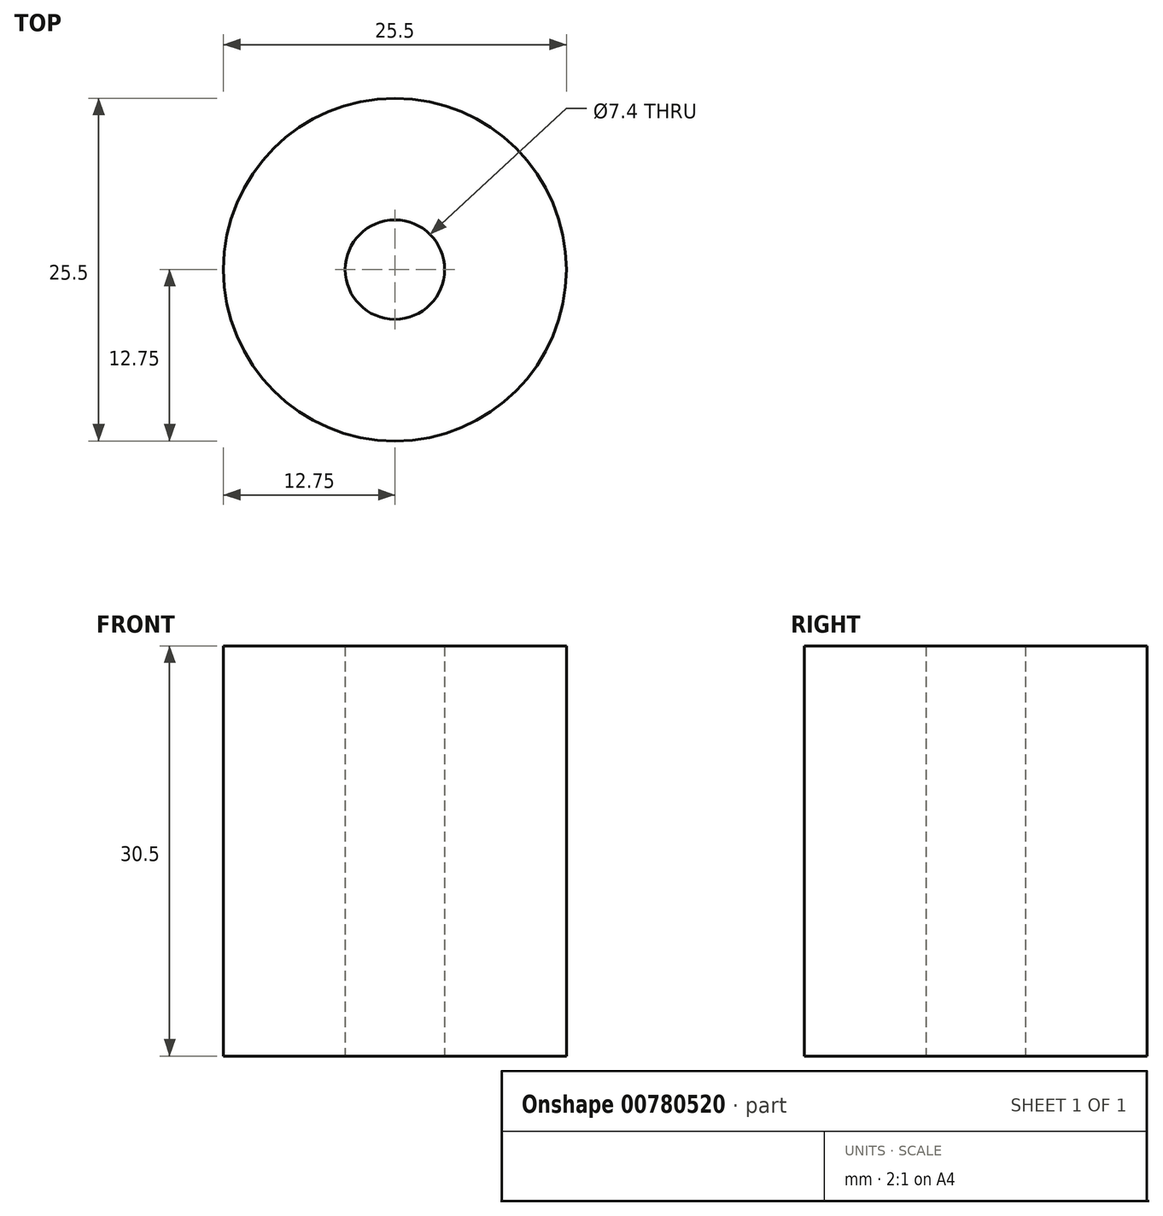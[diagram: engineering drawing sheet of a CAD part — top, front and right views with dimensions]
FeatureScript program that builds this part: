
annotation { "Feature Type Name" : "Feature", "Feature Type Description" : "" }
export const myFeature = defineFeature(function(context is Context, id is Id, definition is map)
    precondition{}
    {
        {
            var Q0;
            Q0=qCreatedBy(makeId("Top.planeOp"),FACE);
            var sketch = newSketch(context, id + "F0", { "sketchPlane" : qUnion([Q0])});
            skCircle(sketch, "E0", {"center": v(0, 0) * mm, "radius": 12.75 * mm});
            skCircle(sketch, "E1", {"center": v(0, 0) * mm, "radius": 3.7 * mm});
            skSolve(sketch);
        }
        {
            var Q0;
            Q0=makeQuery(id+"F0.imprint","IMPRINT",FACE,{"disambiguationData":[TD([[makeQuery(id+"F0.imprint","IMPRINT",EDGE,{"derivedFrom":sQuery(id+"F0.wireOp",EDGE,"E0")}),1.0]])]});
            extrude(context, id + "F1", {"entities" : qUnion([Q0]), "depth" : 30.5 * mm, "offsetDistance" : 25 * mm});
        }
    });
